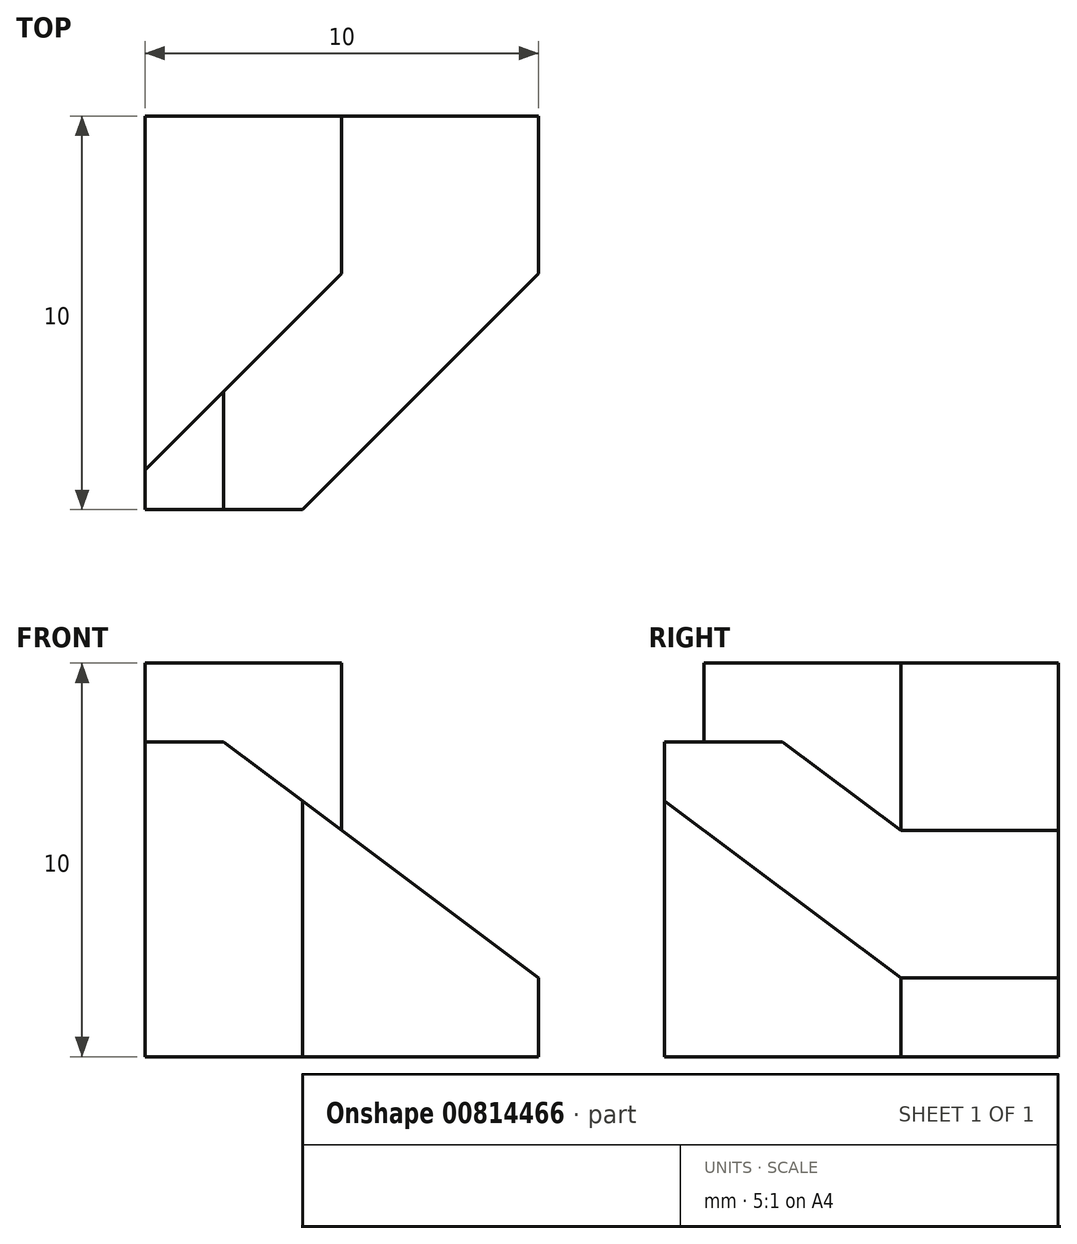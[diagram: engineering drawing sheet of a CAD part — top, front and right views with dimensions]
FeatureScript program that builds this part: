
annotation { "Feature Type Name" : "Feature", "Feature Type Description" : "" }
export const myFeature = defineFeature(function(context is Context, id is Id, definition is map)
    precondition{}
    {
        {
            var Q0;
            Q0=qCreatedBy(makeId("Front.planeOp"),FACE);
            var sketch = newSketch(context, id + "F0", { "sketchPlane" : qUnion([Q0])});
            skLineSegment(sketch, "E0", {"start": v(0, 8) * mm, "end": v(0, 0) * mm});
            skLineSegment(sketch, "E1", {"start": v(0, 0) * mm, "end": v(10, 0) * mm});
            skLineSegment(sketch, "E2", {"start": v(10, 0) * mm, "end": v(10, 2) * mm});
            skLineSegment(sketch, "E3", {"start": v(10, 2) * mm, "end": v(2, 8) * mm});
            skLineSegment(sketch, "E4", {"start": v(2, 8) * mm, "end": v(0, 8) * mm});
            skSolve(sketch);
        }
        {
            var Q0;
            Q0 = qSketchRegion(id + "F0", true);
            extrude(context, id + "F1", {"entities" : qUnion([Q0]), "oppositeDirection" : true, "depth" : 10 * mm, "offsetDistance" : 25 * mm});
        }
        {
            var Q0;
            Q0=makeQuery(id+"F1.opExtrude","SWEPT_FACE",FACE,{"disambiguationData":[OSD([sQuery(id+"F0.wireOp",EDGE,"E1")])]});
            var sketch = newSketch(context, id + "F2", { "sketchPlane" : qUnion([Q0])});
            skLineSegment(sketch, "E5", {"start": v(4, 0) * mm, "end": v(10, -6) * mm});
            skLineSegment(sketch, "E6.0", {"start": v(0, 0) * mm, "end": v(10, 0) * mm});
            skLineSegment(sketch, "E7.0", {"start": v(10, -10) * mm, "end": v(10, 0) * mm});
            skLineSegment(sketch, "E8", {"start": v(5, -10) * mm, "end": v(5, -6) * mm});
            skLineSegment(sketch, "E9", {"start": v(5, -6) * mm, "end": v(0, -1) * mm});
            skLineSegment(sketch, "E10.0", {"start": v(0, -10) * mm, "end": v(0, 0) * mm});
            skLineSegment(sketch, "E11.0", {"start": v(0, -10) * mm, "end": v(10, -10) * mm});
            skSolve(sketch);
        }
        {
            var Q0;
            {var subQ0=sQuery(id+"F2.wireOp",EDGE,"E5");Q0=makeQuery(id+"F2.imprint","IMPRINT",FACE,{"disambiguationData":[TD([[makeQuery(id+"F2.imprint","IMPRINT",EDGE,{"derivedFrom":subQ0}),1.0]])]});}
            extrude(context, id + "F3", {"entities" : qUnion([Q0]), "operationType" : NewBodyOperationType.REMOVE, "endBound" : BoundingType.THROUGH_ALL, "oppositeDirection" : true, "depth" : 25 * mm, "offsetDistance" : 25 * mm});
        }
        {
            var Q0;
            {var subQ0=sQuery(id+"F2.wireOp",EDGE,"E8");Q0=makeQuery(id+"F2.imprint","IMPRINT",FACE,{"disambiguationData":[TD([[makeQuery(id+"F2.imprint","IMPRINT",EDGE,{"derivedFrom":subQ0}),1.0]])]});}
            extrude(context, id + "F4", {"entities" : qUnion([Q0]), "operationType" : NewBodyOperationType.ADD, "oppositeDirection" : true, "depth" : 10 * mm, "offsetDistance" : 25 * mm});
        }
    });
